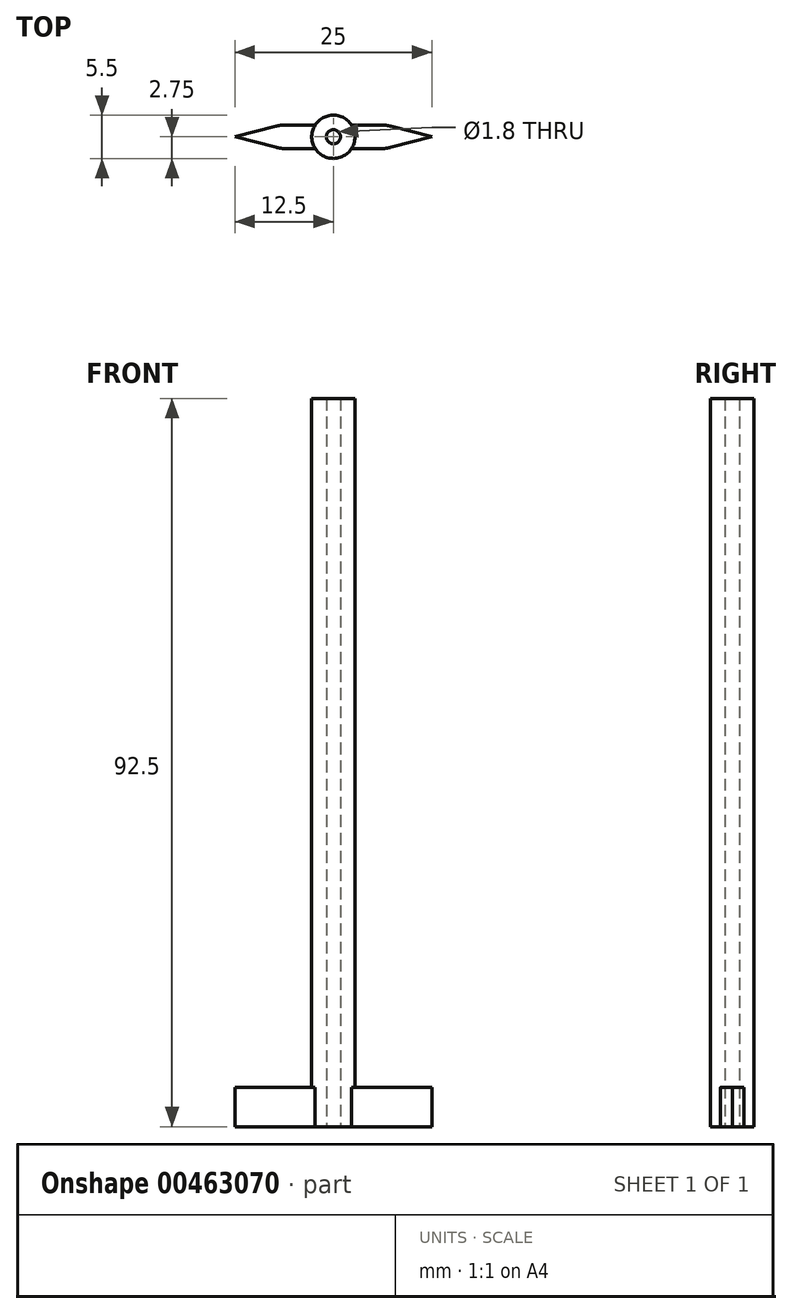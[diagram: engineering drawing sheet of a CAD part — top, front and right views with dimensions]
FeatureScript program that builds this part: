
annotation { "Feature Type Name" : "Feature", "Feature Type Description" : "" }
export const myFeature = defineFeature(function(context is Context, id is Id, definition is map)
    precondition{}
    {
        {
            var Q0;
            Q0=qCreatedBy(makeId("Top.planeOp"),FACE);
            var sketch = newSketch(context, id + "F0", { "sketchPlane" : qUnion([Q0])});
            skCircle(sketch, "E0", {"center": v(0, 0) * mm, "radius": 2.75 * mm});
            skCircle(sketch, "E1", {"center": v(0, 0) * mm, "radius": 0.9 * mm});
            skLineSegment(sketch, "E2.bottom", {"start": v(6.06, 1.5) * mm, "end": v(2.3, 1.5) * mm});
            skLineSegment(sketch, "E2.top", {"start": v(6.06, -1.5) * mm, "end": v(2.3, -1.5) * mm});
            skLineSegment(sketch, "E2.right", {"start": v(-12.5, 0) * mm, "end": v(-12.5, -1.5) * mm});
            skLineSegment(sketch, "E3", {"start": v(-12.5, 0) * mm, "end": v(-7.3, 1.34) * mm});
            skLineSegment(sketch, "E4", {"start": v(-12.5, 0) * mm, "end": v(-7.3, -1.34) * mm});
            skLineSegment(sketch, "E5", {"start": v(12.5, 0) * mm, "end": v(7.3, 1.34) * mm});
            skLineSegment(sketch, "E6", {"start": v(12.5, 0) * mm, "end": v(7.3, -1.34) * mm});
            skPoint(sketch, "E7.orphan", {"position": v(-12.5, 1.5) * mm});
            skPoint(sketch, "E8.orphan", {"position": v(12.5, 1.5) * mm});
            skPoint(sketch, "E2.left.end.orphan", {"position": v(12.5, -1.5) * mm});
            skLineSegment(sketch, "E9.trimOffspring", {"start": v(-2.3, -1.5) * mm, "end": v(-6.06, -1.5) * mm});
            skLineSegment(sketch, "E10.trimOffspring", {"start": v(-2.3, 1.5) * mm, "end": v(-6.06, 1.5) * mm});
            skPoint(sketch, "E11.visualSharp", {"position": v(-6.7, 1.5) * mm});
            skArc(sketch, "E11.filletArc", {"start": v(-6.06, 1.5) * mm, "mid": v(-6.69, 1.46) * mm, "end": v(-7.3, 1.34) * mm});
            skPoint(sketch, "E12.visualSharp", {"position": v(-6.7, -1.5) * mm});
            skArc(sketch, "E12.filletArc", {"start": v(-7.3, -1.34) * mm, "mid": v(-6.69, -1.46) * mm, "end": v(-6.06, -1.5) * mm});
            skPoint(sketch, "E13.visualSharp", {"position": v(6.7, 1.5) * mm});
            skArc(sketch, "E13.filletArc", {"start": v(7.3, 1.34) * mm, "mid": v(6.69, 1.46) * mm, "end": v(6.06, 1.5) * mm});
            skPoint(sketch, "E14.visualSharp", {"position": v(6.7, -1.5) * mm});
            skArc(sketch, "E14.filletArc", {"start": v(6.06, -1.5) * mm, "mid": v(6.69, -1.46) * mm, "end": v(7.3, -1.34) * mm});
            skSolve(sketch);
        }
        {
            var Q0;
            Q0=makeQuery(id+"F0.imprint","IMPRINT",FACE,{"disambiguationData":[TD([[makeQuery(id+"F0.imprint","IMPRINT",EDGE,{"derivedFrom":sQuery(id+"F0.wireOp",EDGE,"E1")}),-1.0]])]});
            var Q1;
            Q1=makeQuery(id+"F0.imprint","IMPRINT",FACE,{"disambiguationData":[TD([[makeQuery(id+"F0.imprint","IMPRINT",EDGE,{"derivedFrom":sQuery(id+"F0.wireOp",EDGE,"E3")}),-1.0]])]});
            var Q2;
            {var subQ1=sQuery(id+"F0.wireOp",EDGE,"E2.bottom");Q2=makeQuery(id+"F0.imprint","IMPRINT",FACE,{"disambiguationData":[TD([[makeQuery(id+"F0.imprint","IMPRINT",EDGE,{"derivedFrom":subQ1}),1.0]])]});}
            extrude(context, id + "F1", {"entities" : qUnion([Q0, Q1, Q2]), "depth" : 5 * mm});
        }
        {
            var Q0;
            Q0=makeQuery(id+"F1.opExtrude","CAP_FACE",FACE,{"disambiguationData":[OSD([sQuery(id+"F0.wireOp",EDGE,"E0"),sQuery(id+"F0.wireOp",EDGE,"E1"),sQuery(id+"F0.wireOp",EDGE,"E2.bottom"),sQuery(id+"F0.wireOp",EDGE,"E2.top"),sQuery(id+"F0.wireOp",EDGE,"E3"),sQuery(id+"F0.wireOp",EDGE,"E4"),sQuery(id+"F0.wireOp",EDGE,"E5"),sQuery(id+"F0.wireOp",EDGE,"E6"),sQuery(id+"F0.wireOp",EDGE,"E9.trimOffspring"),sQuery(id+"F0.wireOp",EDGE,"E10.trimOffspring"),sQuery(id+"F0.wireOp",EDGE,"E11.filletArc"),sQuery(id+"F0.wireOp",EDGE,"E12.filletArc"),sQuery(id+"F0.wireOp",EDGE,"E13.filletArc"),sQuery(id+"F0.wireOp",EDGE,"E14.filletArc")])],"isStart":false});
            var sketch = newSketch(context, id + "F2", { "sketchPlane" : qUnion([Q0])});
            skCircle(sketch, "E15", {"center": v(0, 0) * mm, "radius": 0.9 * mm});
            skCircle(sketch, "E16", {"center": v(0, 0) * mm, "radius": 2.75 * mm});
            skSolve(sketch);
        }
        {
            var Q0;
            Q0 = qSketchRegion(id + "F2", true);
            extrude(context, id + "F3", {"entities" : qUnion([Q0]), "operationType" : NewBodyOperationType.ADD, "depth" : 87.5 * mm, "offsetDistance" : 25 * mm});
        }
    });
